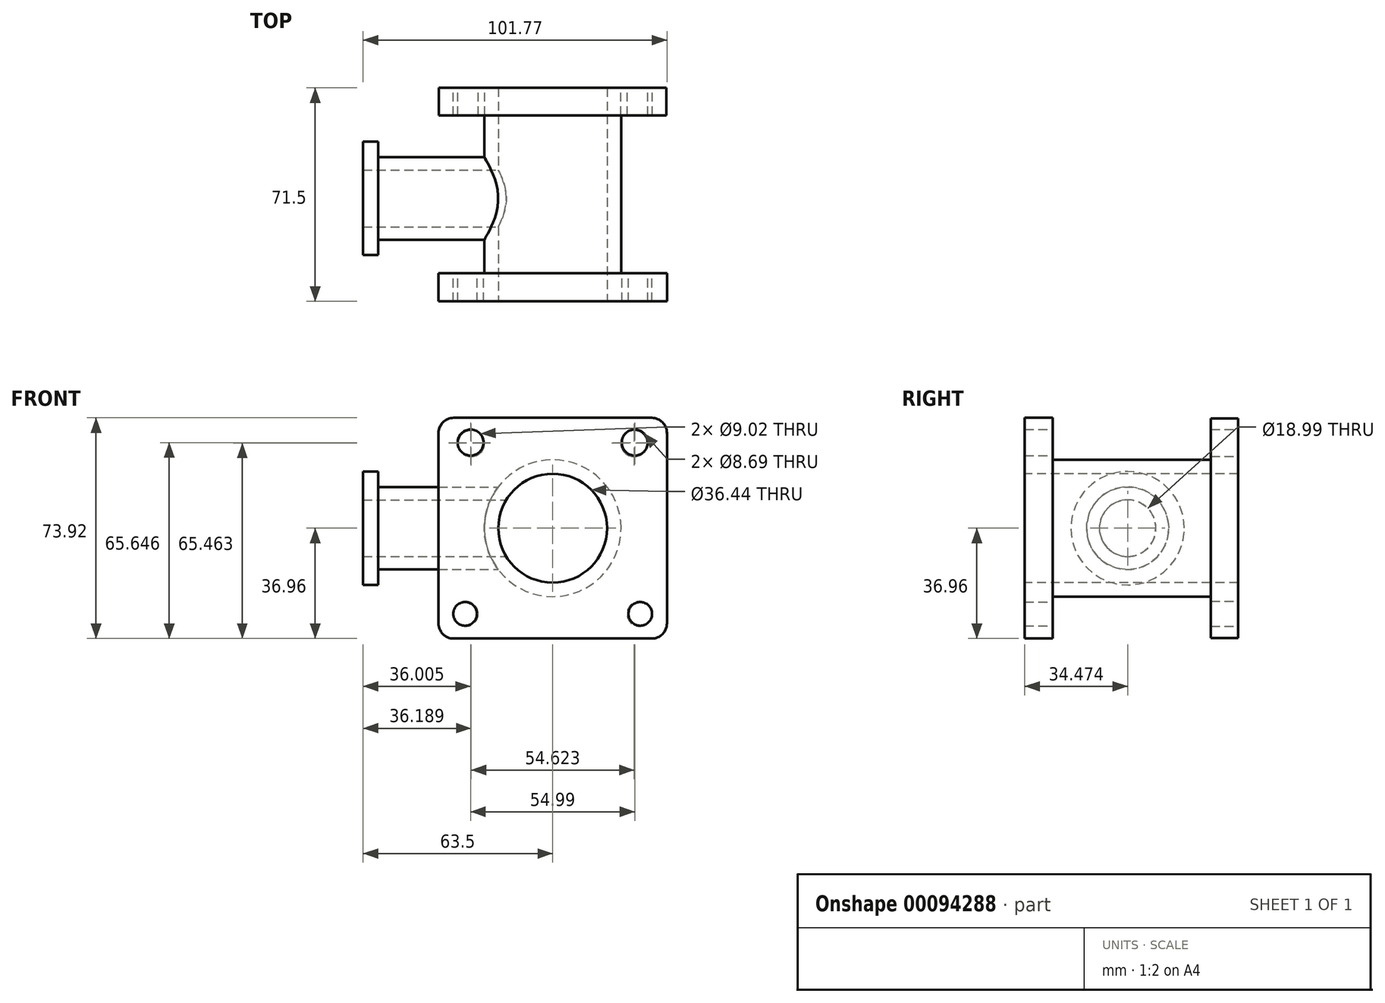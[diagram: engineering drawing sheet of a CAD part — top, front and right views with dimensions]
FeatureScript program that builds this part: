
annotation { "Feature Type Name" : "Feature", "Feature Type Description" : "" }
export const myFeature = defineFeature(function(context is Context, id is Id, definition is map)
    precondition{}
    {
        {
            var Q0;
            Q0=qCreatedBy(makeId("Front.planeOp"),FACE);
            var sketch = newSketch(context, id + "F0", { "sketchPlane" : qUnion([Q0])});
            skLineSegment(sketch, "E0.bottom", {"start": v(38.13, 36.75) * mm, "end": v(-38.13, 36.75) * mm});
            skLineSegment(sketch, "E0.top", {"start": v(38.13, -36.75) * mm, "end": v(-38.13, -36.75) * mm});
            skLineSegment(sketch, "E0.left", {"start": v(38.13, 36.75) * mm, "end": v(38.13, -36.75) * mm});
            skLineSegment(sketch, "E0.right", {"start": v(-38.13, 36.75) * mm, "end": v(-38.13, -36.75) * mm});
            skPoint(sketch, "E0.middle", {"position": v(0, 0) * mm});
            skCircle(sketch, "E1", {"center": v(-27.31, 28.5) * mm, "radius": 4.5 * mm});
            skCircle(sketch, "E2.MirrorC", {"center": v(27.31, 28.5) * mm, "radius": 4.5 * mm});
            skCircle(sketch, "E3", {"center": v(29.14, -28.69) * mm, "radius": 4.18 * mm});
            skCircle(sketch, "E4.MirrorC", {"center": v(-29.14, -28.69) * mm, "radius": 4.18 * mm});
            skSolve(sketch);
        }
        {
            var Q0;
            Q0 = qSketchRegion(id + "F0", true);
            extrude(context, id + "F1", {"entities" : qUnion([Q0]), "depth" : 9.2 * mm});
        }
        {
            var Q0;
            Q0=makeQuery(id+"F1.opExtrude","SWEPT_EDGE",EDGE,{"disambiguationData":[OSD([sQuery(id+"F0.wireOp",EDGE,"E0.bottom"),sQuery(id+"F0.wireOp",EDGE,"E0.left")])]});
            var Q1;
            Q1=makeQuery(id+"F1.opExtrude","SWEPT_EDGE",EDGE,{"disambiguationData":[OSD([sQuery(id+"F0.wireOp",EDGE,"E0.bottom"),sQuery(id+"F0.wireOp",EDGE,"E0.right")])]});
            var Q2;
            Q2=makeQuery(id+"F1.opExtrude","SWEPT_EDGE",EDGE,{"disambiguationData":[OSD([sQuery(id+"F0.wireOp",EDGE,"E0.top"),sQuery(id+"F0.wireOp",EDGE,"E0.right")])]});
            var Q3;
            Q3=makeQuery(id+"F1.opExtrude","SWEPT_EDGE",EDGE,{"disambiguationData":[OSD([sQuery(id+"F0.wireOp",EDGE,"E0.top"),sQuery(id+"F0.wireOp",EDGE,"E0.left")])]});
            fillet(context, id + "F2", {"entities" : qUnion([Q0, Q1, Q2, Q3]), "radius" : 5.08 * mm, "tangentPropagation" : true, "allowEdgeOverflow" : false});
        }
        {
            var Q0;
            Q0=qCreatedBy(makeId("Front.planeOp"),FACE);
            var sketch = newSketch(context, id + "F3", { "sketchPlane" : qUnion([Q0])});
            skCircle(sketch, "E5", {"center": v(0, 0) * mm, "radius": 22.9 * mm});
            skSolve(sketch);
        }
        {
            var Q0;
            Q0 = qSketchRegion(id + "F3", true);
            extrude(context, id + "F4", {"entities" : qUnion([Q0]), "operationType" : NewBodyOperationType.ADD, "depth" : 62.12 * mm});
        }
        {
            var Q0;
            Q0=makeQuery(id+"F4.opExtrude","CAP_FACE",FACE,{"disambiguationData":[OSD([sQuery(id+"F3.wireOp",EDGE,"E5")])],"isStart":false});
            var sketch = newSketch(context, id + "F5", { "sketchPlane" : qUnion([Q0])});
            skLineSegment(sketch, "E6.bottom", {"start": v(38.27, 36.96) * mm, "end": v(-38.27, 36.96) * mm});
            skLineSegment(sketch, "E6.top", {"start": v(38.27, -36.96) * mm, "end": v(-38.27, -36.96) * mm});
            skLineSegment(sketch, "E6.left", {"start": v(38.27, 36.96) * mm, "end": v(38.27, -36.96) * mm});
            skLineSegment(sketch, "E6.right", {"start": v(-38.27, 36.96) * mm, "end": v(-38.27, -36.96) * mm});
            skPoint(sketch, "E6.middle", {"position": v(0, 0) * mm});
            skCircle(sketch, "E7", {"center": v(-27.5, 28.69) * mm, "radius": 4.35 * mm});
            skCircle(sketch, "E8.MirrorC", {"center": v(27.5, 28.69) * mm, "radius": 4.35 * mm});
            skCircle(sketch, "E9", {"center": v(-29.33, -28.69) * mm, "radius": 3.97 * mm});
            skCircle(sketch, "E10.MirrorC", {"center": v(29.33, -28.69) * mm, "radius": 3.97 * mm});
            skSolve(sketch);
        }
        {
            var Q0;
            Q0 = qSketchRegion(id + "F5", true);
            extrude(context, id + "F6", {"entities" : qUnion([Q0]), "operationType" : NewBodyOperationType.ADD, "depth" : 9.38 * mm});
        }
        {
            var Q0;
            Q0=makeQuery(id+"F6.opExtrude","SWEPT_EDGE",EDGE,{"disambiguationData":[OSD([sQuery(id+"F5.wireOp",EDGE,"E6.bottom"),sQuery(id+"F5.wireOp",EDGE,"E6.left")])]});
            var Q1;
            Q1=makeQuery(id+"F6.opExtrude","SWEPT_EDGE",EDGE,{"disambiguationData":[OSD([sQuery(id+"F5.wireOp",EDGE,"E6.bottom"),sQuery(id+"F5.wireOp",EDGE,"E6.right")])]});
            var Q2;
            Q2=makeQuery(id+"F6.opExtrude","SWEPT_EDGE",EDGE,{"disambiguationData":[OSD([sQuery(id+"F5.wireOp",EDGE,"E6.top"),sQuery(id+"F5.wireOp",EDGE,"E6.right")])]});
            var Q3;
            Q3=makeQuery(id+"F6.opExtrude","SWEPT_EDGE",EDGE,{"disambiguationData":[OSD([sQuery(id+"F5.wireOp",EDGE,"E6.top"),sQuery(id+"F5.wireOp",EDGE,"E6.left")])]});
            fillet(context, id + "F7", {"entities" : qUnion([Q0, Q1, Q2, Q3]), "radius" : 5.08 * mm, "tangentPropagation" : true, "allowEdgeOverflow" : false});
        }
        {
            var Q0;
            Q0=makeQuery(id+"F6.opExtrude","CAP_FACE",FACE,{"disambiguationData":[OSD([sQuery(id+"F5.wireOp",EDGE,"E6.bottom"),sQuery(id+"F5.wireOp",EDGE,"E6.top"),sQuery(id+"F5.wireOp",EDGE,"E6.left"),sQuery(id+"F5.wireOp",EDGE,"E6.right"),sQuery(id+"F5.wireOp",EDGE,"E7"),sQuery(id+"F5.wireOp",EDGE,"E8.MirrorC"),sQuery(id+"F5.wireOp",EDGE,"E9"),sQuery(id+"F5.wireOp",EDGE,"E10.MirrorC")])],"isStart":false});
            var sketch = newSketch(context, id + "F8", { "sketchPlane" : qUnion([Q0])});
            skCircle(sketch, "E11", {"center": v(0, 0) * mm, "radius": 18.22 * mm});
            skSolve(sketch);
        }
        {
            var Q0;
            Q0 = qSketchRegion(id + "F8", true);
            extrude(context, id + "F9", {"entities" : qUnion([Q0]), "operationType" : NewBodyOperationType.REMOVE, "endBound" : BoundingType.THROUGH_ALL, "oppositeDirection" : true, "depth" : 25.4 * mm});
        }
        {
            var Q0;
            Q0=qCreatedBy(makeId("Right.planeOp"),FACE);
            var sketch = newSketch(context, id + "F10", { "sketchPlane" : qUnion([Q0])});
            skCircle(sketch, "E12", {"center": v(-37.03, 0) * mm, "radius": 13.83 * mm});
            skSolve(sketch);
        }
        {
            var Q0;
            Q0 = qSketchRegion(id + "F10", true);
            extrude(context, id + "F11", {"entities" : qUnion([Q0]), "operationType" : NewBodyOperationType.ADD, "oppositeDirection" : true, "depth" : 58.42 * mm});
        }
        {
            var Q0;
            Q0 = qSketchRegion(id + "F3", true);
            extrude(context, id + "F12", {"entities" : qUnion([Q0]), "operationType" : NewBodyOperationType.ADD, "depth" : 71.36 * mm});
        }
        {
            var Q0;
            Q0 = qSketchRegion(id + "F8", true);
            extrude(context, id + "F13", {"entities" : qUnion([Q0]), "operationType" : NewBodyOperationType.REMOVE, "endBound" : BoundingType.THROUGH_ALL, "oppositeDirection" : true, "depth" : 25.4 * mm});
        }
        {
            var Q0;
            Q0=makeQuery(id+"F11.opExtrude","CAP_FACE",FACE,{"disambiguationData":[OSD([sQuery(id+"F10.wireOp",EDGE,"E12")])],"isStart":false});
            var sketch = newSketch(context, id + "F14", { "sketchPlane" : qUnion([Q0])});
            skCircle(sketch, "E13", {"center": v(37.03, 0) * mm, "radius": 9.5 * mm});
            skSolve(sketch);
        }
        {
            var Q0;
            Q0=makeQuery(id+"F14.imprint","IMPRINT",FACE,{"disambiguationData":[TD([[makeQuery(id+"F14.imprint","IMPRINT",EDGE,{"derivedFrom":sQuery(id+"F14.wireOp",EDGE,"E13")}),1.0]])]});
            var sketch = newSketch(context, id + "F15", { "sketchPlane" : qUnion([Q0])});
            skCircle(sketch, "E14", {"center": v(37.03, 0) * mm, "radius": 18.99 * mm});
            skSolve(sketch);
        }
        {
            var Q0;
            Q0 = qSketchRegion(id + "F15", true);
            extrude(context, id + "F16", {"entities" : qUnion([Q0]), "operationType" : NewBodyOperationType.ADD, "depth" : 5.08 * mm});
        }
        {
            var Q0;
            Q0 = qSketchRegion(id + "F14", true);
            extrude(context, id + "F17", {"entities" : qUnion([Q0]), "operationType" : NewBodyOperationType.REMOVE, "endBound" : BoundingType.SYMMETRIC, "depth" : 114.23 * mm});
        }
    });
